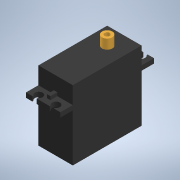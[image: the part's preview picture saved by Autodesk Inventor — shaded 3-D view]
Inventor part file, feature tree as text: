
AUTODESK INVENTOR PART (.ipt)
format: ipt  version: 2020 (Build 240168000, 168)  size: 202,240 bytes
history: native  units: in
note: dims shown in document units (in); Inventor stores cm internally (conversion verified against a paired STEP export)
features: extrude x6, sketch x6, projected_geometry x3, plane x1
ambient origin geometry x8: Origin, YZ Plane, XZ Plane, XY Plane, X Axis, Y Axis, Z Axis, Center Point
bodies: Solid1 (feature_tree)
feature tree (16):
  extrude  "Extrusion1"  Depth=1.5748in
  plane  "Work Plane1"
  extrude  "Extrusion2"  TaperAngle=0.0deg  [1 undecoded]
  extrude  "Extrusion3"  Depth=2.1457in
  extrude  "Extrusion4"  Depth=0.3937in
  extrude  "Extrusion5"  Depth=0.1063in TaperAngle=0.0deg
  extrude  "Extrusion6"  Depth=0.0787in
  sketch  "Sketch1"  dims[d0=0.7874in d1=1.5748in]
  sketch  "Sketch2"  dims[d2=1.0906in d3=0.0in d4=0.0in]
  projected_geometry  "Projected Loop1"
  sketch  "Sketch3"  dims[d5=0.5in d6=0.0in d7=2.1457in]
  projected_geometry  "Projected Loop2"
  sketch  "Sketch4"  dims[d8=0.3937in d9=1.9488in]
  sketch  "Sketch5"  dims[d10=0.1772in d11=0.1063in d12=0.0in]
  projected_geometry  "Projected Loop3"
  sketch  "Sketch6"  dims[d13=0.0984in d14=0.0787in d15=0.1575in d16=0.0787in d17=0.0in d18=0.2362in d19=1.1811in d20=0.2205in d21=0.0in d22=0.1181in d23=0.2205in d24=0.0in]
note: 1 required parameter value undecoded (feature->parameter linkage not recoverable at this tier; creation-order binding heuristic only, values carry confidence <= 0.55)
